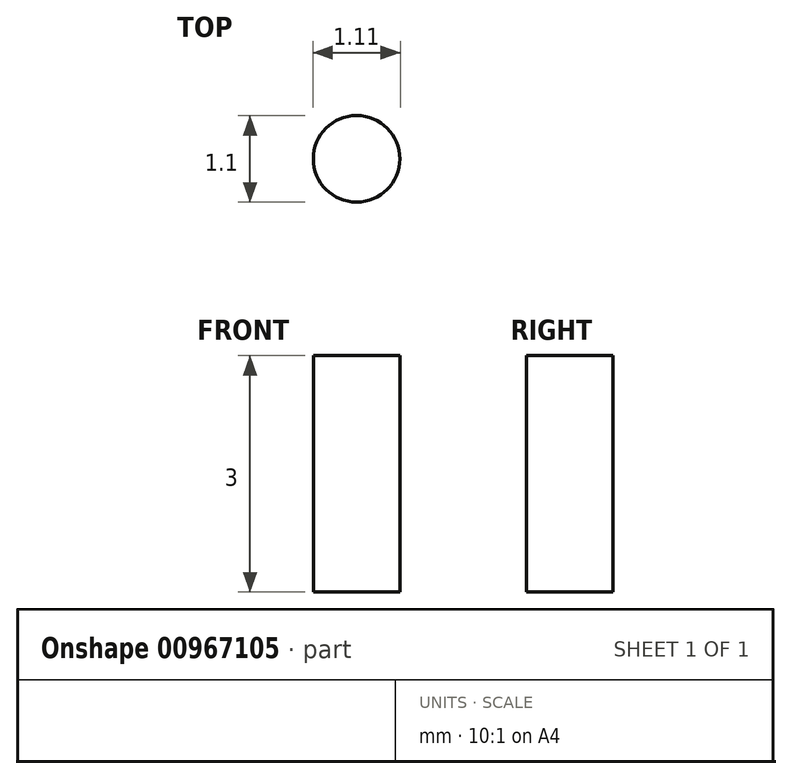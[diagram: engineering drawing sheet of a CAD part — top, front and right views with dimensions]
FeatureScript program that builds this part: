
annotation { "Feature Type Name" : "Feature", "Feature Type Description" : "" }
export const myFeature = defineFeature(function(context is Context, id is Id, definition is map)
    precondition{}
    {
        {
            var Q0;
            Q0=qCreatedBy(makeId("Top.planeOp"),FACE);
            var sketch = newSketch(context, id + "F0", { "sketchPlane" : qUnion([Q0])});
            skCircle(sketch, "E0", {"center": v(-8, 9) * mm, "radius": 0.55 * mm});
            skCircle(sketch, "E1", {"center": v(-8, -9) * mm, "radius": 0.55 * mm});
            skCircle(sketch, "E2", {"center": v(8, 9) * mm, "radius": 0.55 * mm});
            skCircle(sketch, "E3", {"center": v(8, -9) * mm, "radius": 0.55 * mm});
            skArc(sketch, "E4", {"start": v(-10, -4.25) * mm, "mid": v(-9.26, -5) * mm, "end": v(-8.5, -4.25) * mm});
            skArc(sketch, "E5", {"start": v(-8.5, 4.25) * mm, "mid": v(-9.26, 5) * mm, "end": v(-10, 4.25) * mm});
            skLineSegment(sketch, "E6", {"start": v(-10, 4.25) * mm, "end": v(-10, -4.25) * mm});
            skLineSegment(sketch, "E7", {"start": v(-8.5, -4.25) * mm, "end": v(-8.5, 4.25) * mm});
            skEllipticalArc(sketch, "E8", {});
            skEllipticalArc(sketch, "E9", {});
            skLineSegment(sketch, "E10", {"start": v(-10, 26.63) * mm, "end": v(-10, 16.43) * mm});
            skLineSegment(sketch, "E11", {"start": v(-8.5, 16.43) * mm, "end": v(-8.5, 26.63) * mm});
            skEllipticalArc(sketch, "E12", {});
            skEllipticalArc(sketch, "E13", {});
            skLineSegment(sketch, "E14", {"start": v(-10, -26.63) * mm, "end": v(-10, -16.43) * mm});
            skLineSegment(sketch, "E15", {"start": v(-8.5, -16.43) * mm, "end": v(-8.5, -26.63) * mm});
            skArc(sketch, "E16", {"start": v(8.5, -4.25) * mm, "mid": v(9.24, -5) * mm, "end": v(10, -4.25) * mm});
            skArc(sketch, "E17", {"start": v(10, 4.25) * mm, "mid": v(9.24, 5) * mm, "end": v(8.5, 4.25) * mm});
            skLineSegment(sketch, "E18", {"start": v(10, 4.25) * mm, "end": v(10, -4.25) * mm});
            skLineSegment(sketch, "E19", {"start": v(8.5, -4.25) * mm, "end": v(8.5, 4.25) * mm});
            skEllipticalArc(sketch, "E20", {});
            skEllipticalArc(sketch, "E21", {});
            skLineSegment(sketch, "E22", {"start": v(10, 26.63) * mm, "end": v(10, 16.43) * mm});
            skLineSegment(sketch, "E23", {"start": v(8.5, 16.43) * mm, "end": v(8.5, 26.63) * mm});
            skEllipticalArc(sketch, "E24", {});
            skEllipticalArc(sketch, "E25", {});
            skLineSegment(sketch, "E26", {"start": v(10, -26.63) * mm, "end": v(10, -16.43) * mm});
            skLineSegment(sketch, "E27", {"start": v(8.5, -16.43) * mm, "end": v(8.5, -26.63) * mm});
            skCircle(sketch, "E28", {"center": v(7.77, 40.6) * mm, "radius": 1.05 * mm});
            skLineSegment(sketch, "E29", {"start": v(0.86, 44.93) * mm, "end": v(12.55, 42.88) * mm});
            skArc(sketch, "E30", {"start": v(0.86, 44.93) * mm, "mid": v(0, 45) * mm, "end": v(-0.87, 44.93) * mm});
            skArc(sketch, "E31", {"start": v(-2.5, 9.63) * mm, "mid": v(-3.57, 9.19) * mm, "end": v(-4, 8.13) * mm});
            skArc(sketch, "E32", {"start": v(4, 8.13) * mm, "mid": v(3.56, 9.19) * mm, "end": v(2.5, 9.63) * mm});
            skArc(sketch, "E33", {"start": v(2.5, -9.62) * mm, "mid": v(3.56, -9.18) * mm, "end": v(4, -8.12) * mm});
            skArc(sketch, "E34", {"start": v(-4, -8.12) * mm, "mid": v(-3.57, -9.18) * mm, "end": v(-2.5, -9.62) * mm});
            skLineSegment(sketch, "E35", {"start": v(-2.5, 9.63) * mm, "end": v(2.5, 9.63) * mm});
            skLineSegment(sketch, "E36", {"start": v(-2.5, -9.62) * mm, "end": v(2.5, -9.62) * mm});
            skLineSegment(sketch, "E37", {"start": v(-4, -8.12) * mm, "end": v(-4, 8.13) * mm});
            skLineSegment(sketch, "E38", {"start": v(4, 8.13) * mm, "end": v(4, -8.12) * mm});
            skEllipticalArc(sketch, "E39", {});
            skEllipticalArc(sketch, "E40", {});
            skLineSegment(sketch, "E41", {"start": v(-2.5, -15.53) * mm, "end": v(2.5, -15.53) * mm});
            skEllipticalArc(sketch, "E42", {});
            skEllipticalArc(sketch, "E43", {});
            skLineSegment(sketch, "E44", {"start": v(-2.5, -27.53) * mm, "end": v(2.5, -27.53) * mm});
            skLineSegment(sketch, "E45", {"start": v(-4, -17.33) * mm, "end": v(-4, -25.73) * mm});
            skLineSegment(sketch, "E46", {"start": v(4, -25.73) * mm, "end": v(4, -17.33) * mm});
            skEllipticalArc(sketch, "E47", {});
            skEllipticalArc(sketch, "E48", {});
            skLineSegment(sketch, "E49", {"start": v(-2.5, 15.53) * mm, "end": v(2.5, 15.53) * mm});
            skEllipticalArc(sketch, "E50", {});
            skEllipticalArc(sketch, "E51", {});
            skLineSegment(sketch, "E52", {"start": v(-2.5, 27.53) * mm, "end": v(2.5, 27.53) * mm});
            skLineSegment(sketch, "E53", {"start": v(-4, 17.33) * mm, "end": v(-4, 25.73) * mm});
            skLineSegment(sketch, "E54", {"start": v(4, 25.73) * mm, "end": v(4, 17.33) * mm});
            skLineSegment(sketch, "E55", {"start": v(28.97, 41) * mm, "end": v(17.55, 39.7) * mm});
            skArc(sketch, "E56", {"start": v(17.55, 39.7) * mm, "mid": v(17.05, 39.81) * mm, "end": v(16.72, 40.2) * mm});
            skArc(sketch, "E57", {"start": v(16.72, 40.2) * mm, "mid": v(16.6, 40.47) * mm, "end": v(16.43, 40.73) * mm});
            skArc(sketch, "E58", {"start": v(16.43, 40.73) * mm, "mid": v(15.99, 41.3) * mm, "end": v(15.45, 41.77) * mm});
            skArc(sketch, "E59", {"start": v(15.45, 41.77) * mm, "mid": v(14.83, 42.16) * mm, "end": v(14.17, 42.47) * mm});
            skArc(sketch, "E60", {"start": v(14.17, 42.47) * mm, "mid": v(13.37, 42.73) * mm, "end": v(12.55, 42.88) * mm});
            skArc(sketch, "E61", {"start": v(18.56, 29.97) * mm, "mid": v(17.4, 29.55) * mm, "end": v(16.34, 28.95) * mm});
            skArc(sketch, "E62", {"start": v(16.34, 28.95) * mm, "mid": v(15.37, 28.16) * mm, "end": v(14.55, 27.23) * mm});
            skArc(sketch, "E63", {"start": v(14.55, 27.23) * mm, "mid": v(13.88, 26.18) * mm, "end": v(13.4, 25.03) * mm});
            skArc(sketch, "E64", {"start": v(13.4, 25.03) * mm, "mid": v(13.1, 23.8) * mm, "end": v(13, 22.55) * mm});
            skLineSegment(sketch, "E65", {"start": v(-13, -22.55) * mm, "end": v(-13, 22.55) * mm});
            skLineSegment(sketch, "E66", {"start": v(13, 22.55) * mm, "end": v(13, -22.55) * mm});
            skCircle(sketch, "E67", {"center": v(-7.78, 40.6) * mm, "radius": 1.05 * mm});
            skLineSegment(sketch, "E68", {"start": v(-0.87, 44.93) * mm, "end": v(-12.56, 42.88) * mm});
            skArc(sketch, "E69", {"start": v(-12.56, 42.88) * mm, "mid": v(-13.38, 42.73) * mm, "end": v(-14.18, 42.47) * mm});
            skArc(sketch, "E70", {"start": v(-14.18, 42.47) * mm, "mid": v(-14.84, 42.16) * mm, "end": v(-15.46, 41.77) * mm});
            skArc(sketch, "E71", {"start": v(-15.46, 41.77) * mm, "mid": v(-16, 41.3) * mm, "end": v(-16.44, 40.73) * mm});
            skArc(sketch, "E72", {"start": v(-13, 22.55) * mm, "mid": v(-13.1, 23.8) * mm, "end": v(-13.4, 25.03) * mm});
            skArc(sketch, "E73", {"start": v(-13.4, 25.03) * mm, "mid": v(-13.9, 26.18) * mm, "end": v(-14.56, 27.23) * mm});
            skArc(sketch, "E74", {"start": v(-14.56, 27.23) * mm, "mid": v(-15.38, 28.16) * mm, "end": v(-16.35, 28.95) * mm});
            skArc(sketch, "E75", {"start": v(-16.35, 28.95) * mm, "mid": v(-17.41, 29.56) * mm, "end": v(-18.57, 29.98) * mm});
            skCircle(sketch, "E76", {"center": v(7.77, -40.6) * mm, "radius": 1.05 * mm});
            skLineSegment(sketch, "E77", {"start": v(0.86, -44.92) * mm, "end": v(12.55, -42.88) * mm});
            skArc(sketch, "E78", {"start": v(-0.87, -44.92) * mm, "mid": v(0, -45) * mm, "end": v(0.86, -44.92) * mm});
            skLineSegment(sketch, "E79", {"start": v(28.98, -41) * mm, "end": v(17.42, -39.7) * mm});
            skArc(sketch, "E80", {"start": v(17.42, -39.7) * mm, "mid": v(16.98, -39.77) * mm, "end": v(16.65, -40.07) * mm});
            skArc(sketch, "E81", {"start": v(16.65, -40.07) * mm, "mid": v(14.9, -41.92) * mm, "end": v(12.55, -42.88) * mm});
            skArc(sketch, "E82", {"start": v(13, -22.55) * mm, "mid": v(13.1, -23.8) * mm, "end": v(13.4, -25.03) * mm});
            skArc(sketch, "E83", {"start": v(13.4, -25.03) * mm, "mid": v(13.88, -26.17) * mm, "end": v(14.55, -27.23) * mm});
            skArc(sketch, "E84", {"start": v(14.55, -27.23) * mm, "mid": v(15.37, -28.16) * mm, "end": v(16.34, -28.95) * mm});
            skArc(sketch, "E85", {"start": v(16.34, -28.95) * mm, "mid": v(17.4, -29.55) * mm, "end": v(18.56, -29.97) * mm});
            skCircle(sketch, "E86", {"center": v(-7.78, -40.6) * mm, "radius": 1.05 * mm});
            skLineSegment(sketch, "E87", {"start": v(-0.87, -44.92) * mm, "end": v(-12.56, -42.88) * mm});
            skArc(sketch, "E88", {"start": v(-16.44, -40.73) * mm, "mid": v(-16, -41.3) * mm, "end": v(-15.46, -41.77) * mm});
            skArc(sketch, "E89", {"start": v(-15.46, -41.77) * mm, "mid": v(-14.84, -42.16) * mm, "end": v(-14.18, -42.47) * mm});
            skArc(sketch, "E90", {"start": v(-14.18, -42.47) * mm, "mid": v(-13.38, -42.72) * mm, "end": v(-12.56, -42.88) * mm});
            skArc(sketch, "E91", {"start": v(-18.57, -29.98) * mm, "mid": v(-17.42, -29.56) * mm, "end": v(-16.35, -28.95) * mm});
            skArc(sketch, "E92", {"start": v(-16.35, -28.95) * mm, "mid": v(-15.38, -28.16) * mm, "end": v(-14.56, -27.23) * mm});
            skArc(sketch, "E93", {"start": v(-14.56, -27.23) * mm, "mid": v(-13.9, -26.18) * mm, "end": v(-13.4, -25.03) * mm});
            skArc(sketch, "E94", {"start": v(-13.4, -25.03) * mm, "mid": v(-13.1, -23.8) * mm, "end": v(-13, -22.55) * mm});
            skLineSegment(sketch, "E95", {"start": v(-30.47, 33.25) * mm, "end": v(-18.57, 29.98) * mm});
            skArc(sketch, "E96", {"start": v(-31.45, 42.93) * mm, "mid": v(-30.49, 41.6) * mm, "end": v(-28.98, 41) * mm});
            skLineSegment(sketch, "E97", {"start": v(-33.54, 44.8) * mm, "end": v(-44.02, 46.55) * mm});
            skArc(sketch, "E98", {"start": v(-44.02, 46.55) * mm, "mid": v(-44.27, 46.55) * mm, "end": v(-44.5, 46.48) * mm});
            skArc(sketch, "E99", {"start": v(-44.5, 46.48) * mm, "mid": v(-48.87, 40.8) * mm, "end": v(-46.95, 33.91) * mm});
            skArc(sketch, "E100", {"start": v(-46.95, 33.91) * mm, "mid": v(-46.76, 33.76) * mm, "end": v(-46.53, 33.67) * mm});
            skLineSegment(sketch, "E101", {"start": v(-46.53, 33.67) * mm, "end": v(-37.86, 31.77) * mm});
            skArc(sketch, "E102", {"start": v(-37.86, 31.77) * mm, "mid": v(-35.34, 31.76) * mm, "end": v(-33.03, 32.78) * mm});
            skArc(sketch, "E103", {"start": v(-33.03, 32.78) * mm, "mid": v(-31.8, 33.31) * mm, "end": v(-30.47, 33.25) * mm});
            skArc(sketch, "E104", {"start": v(-31.45, 42.93) * mm, "mid": v(-32.27, 44.12) * mm, "end": v(-33.54, 44.8) * mm});
            skLineSegment(sketch, "E105", {"start": v(-28.98, 41) * mm, "end": v(-17.56, 39.7) * mm});
            skArc(sketch, "E106", {"start": v(-17.56, 39.7) * mm, "mid": v(-17.06, 39.81) * mm, "end": v(-16.73, 40.2) * mm});
            skArc(sketch, "E107", {"start": v(-16.73, 40.2) * mm, "mid": v(-16.6, 40.47) * mm, "end": v(-16.44, 40.73) * mm});
            skCircle(sketch, "E108", {"center": v(-38.9, 38.9) * mm, "radius": 5 * mm});
            skLineSegment(sketch, "E109", {"start": v(34, 44.87) * mm, "end": v(44.02, 46.55) * mm});
            skArc(sketch, "E110", {"start": v(44.02, 46.55) * mm, "mid": v(44.27, 46.55) * mm, "end": v(44.5, 46.48) * mm});
            skArc(sketch, "E111", {"start": v(44.5, 46.48) * mm, "mid": v(48.86, 40.8) * mm, "end": v(46.95, 33.91) * mm});
            skArc(sketch, "E112", {"start": v(46.95, 33.91) * mm, "mid": v(46.75, 33.76) * mm, "end": v(46.52, 33.67) * mm});
            skLineSegment(sketch, "E113", {"start": v(46.52, 33.67) * mm, "end": v(37.85, 31.77) * mm});
            skArc(sketch, "E114", {"start": v(37.85, 31.77) * mm, "mid": v(35.33, 31.76) * mm, "end": v(33.03, 32.78) * mm});
            skArc(sketch, "E115", {"start": v(33.03, 32.78) * mm, "mid": v(31.8, 33.31) * mm, "end": v(30.46, 33.25) * mm});
            skLineSegment(sketch, "E116", {"start": v(30.46, 33.25) * mm, "end": v(18.56, 29.97) * mm});
            skArc(sketch, "E117", {"start": v(28.97, 41) * mm, "mid": v(30.49, 41.6) * mm, "end": v(31.45, 42.92) * mm});
            skArc(sketch, "E118", {"start": v(34, 44.87) * mm, "mid": v(32.44, 44.26) * mm, "end": v(31.45, 42.92) * mm});
            skCircle(sketch, "E119", {"center": v(38.89, 38.9) * mm, "radius": 5 * mm});
            skCircle(sketch, "E120", {"center": v(38.9, -38.89) * mm, "radius": 5 * mm});
            skLineSegment(sketch, "E121", {"start": v(33.54, -44.8) * mm, "end": v(44.03, -46.55) * mm});
            skArc(sketch, "E122", {"start": v(44.03, -46.55) * mm, "mid": v(44.27, -46.55) * mm, "end": v(44.5, -46.48) * mm});
            skArc(sketch, "E123", {"start": v(44.5, -46.48) * mm, "mid": v(48.87, -40.8) * mm, "end": v(46.95, -33.91) * mm});
            skArc(sketch, "E124", {"start": v(46.95, -33.91) * mm, "mid": v(46.76, -33.76) * mm, "end": v(46.53, -33.67) * mm});
            skLineSegment(sketch, "E125", {"start": v(46.53, -33.67) * mm, "end": v(37.86, -31.77) * mm});
            skArc(sketch, "E126", {"start": v(37.86, -31.77) * mm, "mid": v(35.34, -31.76) * mm, "end": v(33.03, -32.78) * mm});
            skArc(sketch, "E127", {"start": v(33.03, -32.78) * mm, "mid": v(31.8, -33.31) * mm, "end": v(30.47, -33.25) * mm});
            skLineSegment(sketch, "E128", {"start": v(30.47, -33.25) * mm, "end": v(18.56, -29.97) * mm});
            skArc(sketch, "E129", {"start": v(31.46, -42.93) * mm, "mid": v(30.5, -41.6) * mm, "end": v(28.98, -41) * mm});
            skArc(sketch, "E130", {"start": v(31.46, -42.93) * mm, "mid": v(32.27, -44.12) * mm, "end": v(33.54, -44.8) * mm});
            skCircle(sketch, "E131", {"center": v(-38.9, -38.89) * mm, "radius": 5 * mm});
            skLineSegment(sketch, "E132", {"start": v(-34, -44.87) * mm, "end": v(-44.03, -46.55) * mm});
            skArc(sketch, "E133", {"start": v(-44.03, -46.55) * mm, "mid": v(-44.27, -46.55) * mm, "end": v(-44.5, -46.48) * mm});
            skArc(sketch, "E134", {"start": v(-44.5, -46.48) * mm, "mid": v(-48.87, -40.8) * mm, "end": v(-46.95, -33.91) * mm});
            skArc(sketch, "E135", {"start": v(-46.95, -33.91) * mm, "mid": v(-46.76, -33.76) * mm, "end": v(-46.53, -33.67) * mm});
            skLineSegment(sketch, "E136", {"start": v(-46.53, -33.67) * mm, "end": v(-37.86, -31.77) * mm});
            skArc(sketch, "E137", {"start": v(-37.86, -31.77) * mm, "mid": v(-35.34, -31.76) * mm, "end": v(-33.03, -32.78) * mm});
            skArc(sketch, "E138", {"start": v(-33.03, -32.78) * mm, "mid": v(-31.8, -33.31) * mm, "end": v(-30.47, -33.25) * mm});
            skLineSegment(sketch, "E139", {"start": v(-30.47, -33.25) * mm, "end": v(-18.57, -29.98) * mm});
            skArc(sketch, "E140", {"start": v(-28.98, -41) * mm, "mid": v(-30.5, -41.6) * mm, "end": v(-31.46, -42.93) * mm});
            skArc(sketch, "E141", {"start": v(-34, -44.87) * mm, "mid": v(-32.45, -44.26) * mm, "end": v(-31.46, -42.93) * mm});
            skLineSegment(sketch, "E142", {"start": v(-28.98, -41) * mm, "end": v(-17.56, -39.7) * mm});
            skArc(sketch, "E143", {"start": v(-17.56, -39.7) * mm, "mid": v(-17.06, -39.81) * mm, "end": v(-16.73, -40.2) * mm});
            skArc(sketch, "E144", {"start": v(-16.73, -40.2) * mm, "mid": v(-16.6, -40.47) * mm, "end": v(-16.44, -40.73) * mm});
            skCircle(sketch, "E145", {"center": v(11, -13.3) * mm, "radius": 1.05 * mm});
            skCircle(sketch, "E146", {"center": v(-11, -13.3) * mm, "radius": 1.05 * mm});
            skCircle(sketch, "E147", {"center": v(0, 35.3) * mm, "radius": 1.05 * mm});
            skEllipticalArc(sketch, "E148", {});
            skEllipticalArc(sketch, "E149", {});
            skLineSegment(sketch, "E150", {"start": v(-5.1, -32.46) * mm, "end": v(5.1, -32.48) * mm});
            skLineSegment(sketch, "E151", {"start": v(5.1, -30.98) * mm, "end": v(-5.1, -30.96) * mm});
            skCircle(sketch, "E152", {"center": v(-31.53, 37.48) * mm, "radius": 1.05 * mm});
            skCircle(sketch, "E153", {"center": v(-46.26, 40.3) * mm, "radius": 1.05 * mm});
            skCircle(sketch, "E154", {"center": v(46.26, 40.3) * mm, "radius": 1.05 * mm});
            skCircle(sketch, "E155", {"center": v(31.53, 37.48) * mm, "radius": 1.05 * mm});
            skCircle(sketch, "E156", {"center": v(31.53, -37.48) * mm, "radius": 1.05 * mm});
            skCircle(sketch, "E157", {"center": v(46.26, -40.3) * mm, "radius": 1.05 * mm});
            skCircle(sketch, "E158", {"center": v(-31.53, -37.48) * mm, "radius": 1.05 * mm});
            skCircle(sketch, "E159", {"center": v(-46.26, -40.3) * mm, "radius": 1.05 * mm});
            const initialGuessF0  = {"E8": [-0.009255, 0.016431643000000003, 0, -0.9, 0.0009, 0.00075, 4.712389, 7.853982], "E9": [-0.009255, 0.026631643, 0, -0.9, 0.0009, 0.00075, 1.570796, 4.712389], "E12": [-0.009255, -0.01642969, 0, -0.9, 0.0009, 0.00075, 1.570796, 4.712389], "E13": [-0.009255, -0.02662969, 0, -0.9, 0.0009, 0.00075, 4.712389, 7.853982], "E20": [0.009245, 0.016431643000000003, 0, -0.9, 0.0009, 0.00075, 4.712389, 7.853982], "E21": [0.009245, 0.026631643, 0, -0.9, 0.0009, 0.00075, 1.570796, 4.712389], "E24": [0.009245, -0.01642969, 0, -0.9, 0.0009, 0.00075, 1.570796, 4.712389], "E25": [0.009245, -0.02662969, 0, -0.9, 0.0009, 0.00075, 4.712389, 7.853982], "E39": [-0.002505, -0.01732969, 0, -1.8, 0.0018, 0.0015, 3.141593, 4.712389], "E40": [0.002495, -0.01732969, 0, -1.8, 0.0018, 0.0015, 1.570796, 3.141593], "E42": [-0.002505, -0.025729690000000003, 0, -1.8, 0.0018, 0.0015, 4.712389, 6.283185], "E43": [0.002495, -0.025729690000000003, 0, -1.8, 0.0018, 0.0015, 0, 1.570796], "E47": [-0.002505, 0.017331643, 0, -1.8, 0.0018, 0.0015, 4.712389, 6.283185], "E48": [0.002495, 0.017331643, 0, -1.8, 0.0018, 0.0015, 0, 1.570796], "E50": [-0.002505, 0.025731643, 0, -1.8, 0.0018, 0.0015, 3.141593, 4.712389], "E51": [0.002495, 0.025731643, 0, -1.8, 0.0018, 0.0015, 1.570796, 3.141593], "E148": [0.005094987, -0.031727787, 0.899998, -0.002007, 0.0009, 0.00075, -1.570796, 1.570796], "E149": [-0.005104987, -0.031705043, 0.899998, -0.002007, 0.0009, 0.00075, 1.570796, 4.712389]};
            skSetInitialGuess(sketch, initialGuessF0);
            skSolve(sketch);
        }
        {
            var Q0;
            Q0=makeQuery(id+"F0.imprint","IMPRINT",FACE,{"disambiguationData":[TD([[makeQuery(id+"F0.imprint","IMPRINT",EDGE,{"derivedFrom":sQuery(id+"F0.wireOp",EDGE,"E0")}),1.0]])]});
            extrude(context, id + "F1", {"entities" : qUnion([Q0]), "depth" : 3 * mm});
        }
    });
